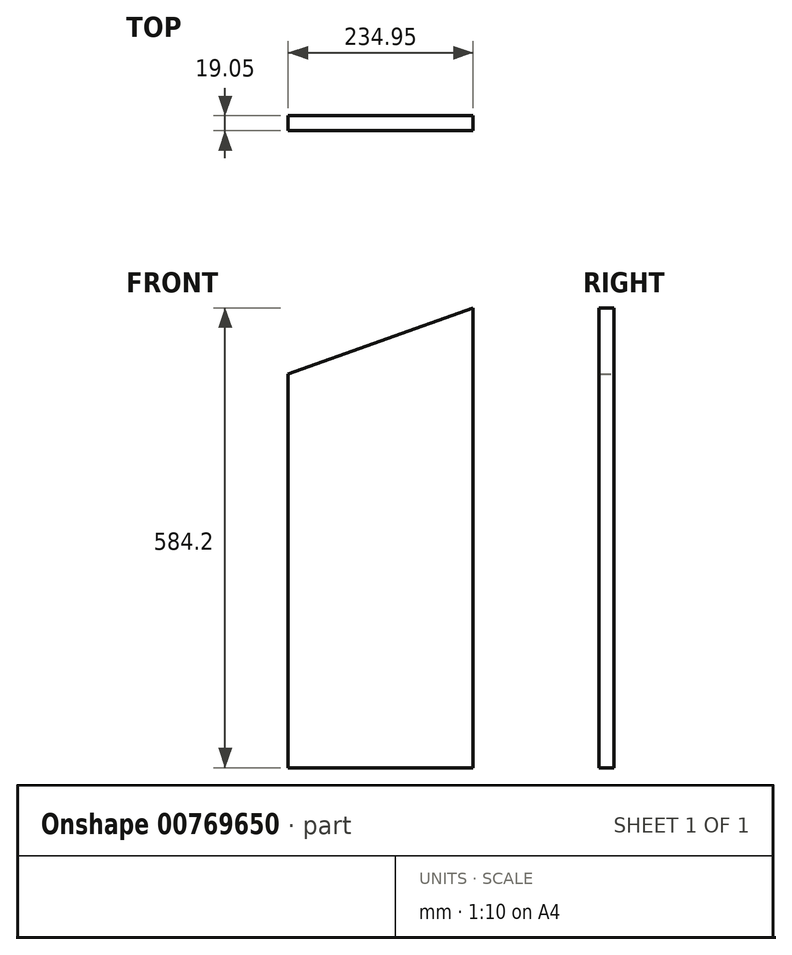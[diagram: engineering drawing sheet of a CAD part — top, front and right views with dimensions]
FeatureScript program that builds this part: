
annotation { "Feature Type Name" : "Feature", "Feature Type Description" : "" }
export const myFeature = defineFeature(function(context is Context, id is Id, definition is map)
    precondition{}
    {
        {
            var Q0;
            Q0=qCreatedBy(makeId("Front.planeOp"),FACE);
            var sketch = newSketch(context, id + "F0", { "sketchPlane" : qUnion([Q0])});
            skLineSegment(sketch, "E0.bottom", {"start": v(-168.57, 499.92) * mm, "end": v(66.38, 499.92) * mm});
            skLineSegment(sketch, "E0.top", {"start": v(-168.57, -84.28) * mm, "end": v(66.38, -84.28) * mm});
            skLineSegment(sketch, "E0.left", {"start": v(-168.57, 499.92) * mm, "end": v(-168.57, -84.28) * mm});
            skLineSegment(sketch, "E0.right", {"start": v(66.38, 499.92) * mm, "end": v(66.38, -84.28) * mm});
            skLineSegment(sketch, "E1", {"start": v(66.38, 499.92) * mm, "end": v(-168.57, 415.66) * mm});
            skSolve(sketch);
        }
        {
            var Q0;
            {var subQ0=sQuery(id+"F0.wireOp",EDGE,"E0.top");Q0=makeQuery(id+"F0.imprint","IMPRINT",FACE,{"disambiguationData":[TD([[makeQuery(id+"F0.imprint","IMPRINT",EDGE,{"derivedFrom":subQ0}),1.0]])]});}
            extrude(context, id + "F1", {"entities" : qUnion([Q0]), "depth" : 19.05 * mm, "offsetDistance" : 25.4 * mm});
        }
        {
            var Q0;
            {var subQ0=sQuery(id+"F0.wireOp",EDGE,"E0.top");Q0=makeQuery(id+"F0.imprint","IMPRINT",FACE,{"disambiguationData":[TD([[makeQuery(id+"F0.imprint","IMPRINT",EDGE,{"derivedFrom":subQ0}),1.0]])]});}
            extrude(context, id + "F2", {"entities" : qUnion([Q0]), "operationType" : NewBodyOperationType.ADD, "depth" : 19.05 * mm, "offsetDistance" : 25.4 * mm});
        }
    });
